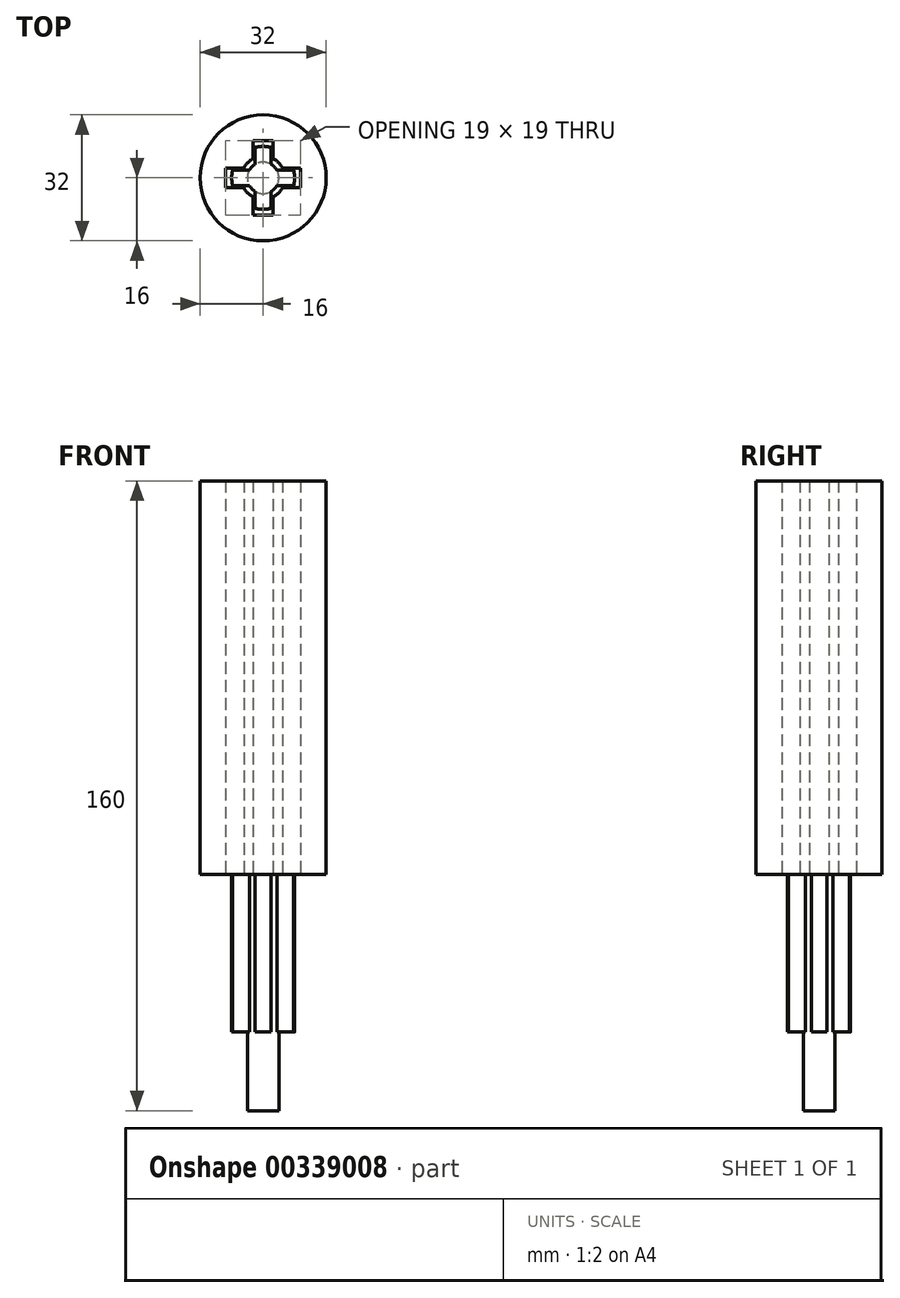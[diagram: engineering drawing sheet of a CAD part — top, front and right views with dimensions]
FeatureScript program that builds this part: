
annotation { "Feature Type Name" : "Feature", "Feature Type Description" : "" }
export const myFeature = defineFeature(function(context is Context, id is Id, definition is map)
    precondition{}
    {
        {
            var Q0;
            Q0=qCreatedBy(makeId("Top.planeOp"),FACE);
            var sketch = newSketch(context, id + "F0", { "sketchPlane" : qUnion([Q0])});
            skCircle(sketch, "E0", {"center": v(0, 0) * mm, "radius": 4 * mm});
            skSolve(sketch);
        }
        {
            var Q0;
            Q0=makeQuery(id+"F0.imprint","IMPRINT",FACE,{"disambiguationData":[TD([[makeQuery(id+"F0.imprint","IMPRINT",EDGE,{"derivedFrom":sQuery(id+"F0.wireOp",EDGE,"E0")}),1.0]])]});
            extrude(context, id + "F1", {"entities" : qUnion([Q0]), "depth" : 20 * mm});
        }
        {
            var Q0;
            Q0=makeQuery(id+"F1.opExtrude","CAP_FACE",FACE,{"disambiguationData":[OSD([sQuery(id+"F0.wireOp",EDGE,"E0")])],"isStart":false});
            cPlane(context, id + "F2", {"entities" : qUnion([Q0]), "cplaneType" : CPlaneType.OFFSET, "offset" : 0 * mm, "width" : 150 * mm, "height" : 150 * mm});
        }
        {
            var Q0;
            Q0=qCreatedBy(id+"F2.planeOp",FACE);
            var sketch = newSketch(context, id + "F3", { "sketchPlane" : qUnion([Q0])});
            skCircle(sketch, "E1", {"center": v(0, 0) * mm, "radius": 8 * mm, "construction": true});
            skCircle(sketch, "E2.0", {"center": v(0, 0) * mm, "radius": 4 * mm});
            skLineSegment(sketch, "E3", {"start": v(0, 4) * mm, "end": v(0, 8) * mm, "construction": true});
            skLineSegment(sketch, "E4", {"start": v(-2, 7.75) * mm, "end": v(-2, 3.46) * mm});
            skLineSegment(sketch, "E5.MirrorCS", {"start": v(2, 7.75) * mm, "end": v(2, 3.46) * mm});
            skLineSegment(sketch, "E6.1.1", {"start": v(-7.75, -2) * mm, "end": v(-3.46, -2) * mm});
            skLineSegment(sketch, "E6.1.3", {"start": v(-4, 0) * mm, "end": v(-8, 0) * mm, "construction": true});
            skLineSegment(sketch, "E6.1.4", {"start": v(-7.75, 2) * mm, "end": v(-3.46, 2) * mm});
            skLineSegment(sketch, "E6.2.1", {"start": v(2, -7.75) * mm, "end": v(2, -3.46) * mm});
            skLineSegment(sketch, "E6.2.3", {"start": v(0, -4) * mm, "end": v(0, -8) * mm, "construction": true});
            skLineSegment(sketch, "E6.2.4", {"start": v(-2, -7.75) * mm, "end": v(-2, -3.46) * mm});
            skLineSegment(sketch, "E6.3.1", {"start": v(7.75, 2) * mm, "end": v(3.46, 2) * mm});
            skLineSegment(sketch, "E6.3.3", {"start": v(4, 0) * mm, "end": v(8, 0) * mm, "construction": true});
            skLineSegment(sketch, "E6.3.4", {"start": v(7.75, -2) * mm, "end": v(3.46, -2) * mm});
            skArc(sketch, "E7", {"start": v(2, 7.75) * mm, "mid": v(0, 8) * mm, "end": v(-2, 7.75) * mm});
            skArc(sketch, "E8", {"start": v(7.75, -2) * mm, "mid": v(8, 0) * mm, "end": v(7.75, 2) * mm});
            skArc(sketch, "E9", {"start": v(-7.75, 2) * mm, "mid": v(-8, 0) * mm, "end": v(-7.75, -2) * mm});
            skArc(sketch, "E10", {"start": v(-2, -7.75) * mm, "mid": v(0, -8) * mm, "end": v(2, -7.75) * mm});
            skPoint(sketch, "E11.orphan", {"position": v(2, -8) * mm});
            skPoint(sketch, "E12.orphan", {"position": v(-2, -8) * mm});
            skPoint(sketch, "E13.orphan", {"position": v(8, -2) * mm});
            skPoint(sketch, "E14.orphan", {"position": v(8, 2) * mm});
            skPoint(sketch, "E15.orphan", {"position": v(2, 8) * mm});
            skPoint(sketch, "E16.MirrorCS.start.orphan", {"position": v(0, 8) * mm});
            skPoint(sketch, "E17.orphan", {"position": v(-2, 8) * mm});
            skPoint(sketch, "E18.orphan", {"position": v(-8, 2) * mm});
            skPoint(sketch, "E6.1.2.end.orphan", {"position": v(-8, -2) * mm});
            skSolve(sketch);
        }
        {
            var Q0;
            {var subQ0=sQuery(id+"F3.wireOp",EDGE,"E6.1.1");Q0=makeQuery(id+"F3.imprint","IMPRINT",FACE,{"disambiguationData":[TD([[makeQuery(id+"F3.imprint","IMPRINT",EDGE,{"derivedFrom":subQ0}),1.0]])]});}
            var Q1;
            {var subQ0=sQuery(id+"F3.wireOp",EDGE,"E2.0");var subQ4=makeQuery(id+"F3.imprint","INTERSECT",VERTEX,{"derivedFrom":[subQ0,sQuery(id+"F3.wireOp",EDGE,"E5.MirrorCS")]});Q1=makeQuery(id+"F3.imprint","IMPRINT",FACE,{"disambiguationData":[TD([[makeQuery(id+"F3.imprint","IMPRINT",EDGE,{"disambiguationData":[TD([[subQ4,1.0]])],"derivedFrom":subQ0}),1.0]])]});}
            var Q2;
            {var subQ0=sQuery(id+"F3.wireOp",EDGE,"E4");Q2=makeQuery(id+"F3.imprint","IMPRINT",FACE,{"disambiguationData":[TD([[makeQuery(id+"F3.imprint","IMPRINT",EDGE,{"derivedFrom":subQ0}),1.0]])]});}
            var Q3;
            {var subQ0=sQuery(id+"F3.wireOp",EDGE,"E6.3.1");Q3=makeQuery(id+"F3.imprint","IMPRINT",FACE,{"disambiguationData":[TD([[makeQuery(id+"F3.imprint","IMPRINT",EDGE,{"derivedFrom":subQ0}),1.0]])]});}
            var Q4;
            {var subQ0=sQuery(id+"F3.wireOp",EDGE,"E6.2.1");Q4=makeQuery(id+"F3.imprint","IMPRINT",FACE,{"disambiguationData":[TD([[makeQuery(id+"F3.imprint","IMPRINT",EDGE,{"derivedFrom":subQ0}),1.0]])]});}
            extrude(context, id + "F4", {"entities" : qUnion([Q0, Q1, Q2, Q3, Q4]), "operationType" : NewBodyOperationType.ADD, "depth" : 40 * mm});
        }
        {
            var Q0;
            Q0=makeQuery(id+"F4.opExtrude","CAP_FACE",FACE,{"disambiguationData":[OSD([sQuery(id+"F3.wireOp",EDGE,"E2.0"),sQuery(id+"F3.wireOp",EDGE,"E4"),sQuery(id+"F3.wireOp",EDGE,"E5.MirrorCS"),sQuery(id+"F3.wireOp",EDGE,"E6.1.1"),sQuery(id+"F3.wireOp",EDGE,"E6.1.4"),sQuery(id+"F3.wireOp",EDGE,"E6.2.1"),sQuery(id+"F3.wireOp",EDGE,"E6.2.4"),sQuery(id+"F3.wireOp",EDGE,"E6.3.1"),sQuery(id+"F3.wireOp",EDGE,"E6.3.4"),sQuery(id+"F3.wireOp",EDGE,"E7"),sQuery(id+"F3.wireOp",EDGE,"E8"),sQuery(id+"F3.wireOp",EDGE,"E9"),sQuery(id+"F3.wireOp",EDGE,"E10")])],"isStart":false});
            cPlane(context, id + "F5", {"entities" : qUnion([Q0]), "cplaneType" : CPlaneType.OFFSET, "offset" : 0 * mm, "width" : 150 * mm, "height" : 150 * mm});
        }
        {
            var Q0;
            Q0=qCreatedBy(id+"F5.planeOp",FACE);
            var sketch = newSketch(context, id + "F6", { "sketchPlane" : qUnion([Q0])});
            skCircle(sketch, "E19", {"center": v(0, 0) * mm, "radius": 16 * mm});
            skCircle(sketch, "E20", {"center": v(0, 0) * mm, "radius": 5.5 * mm});
            skLineSegment(sketch, "E21", {"start": v(0, 5.5) * mm, "end": v(0, 9.5) * mm, "construction": true});
            skLineSegment(sketch, "E22", {"start": v(0, 9.5) * mm, "end": v(-2.5, 9.5) * mm});
            skLineSegment(sketch, "E23", {"start": v(-2.5, 9.5) * mm, "end": v(-2.5, 4.9) * mm});
            skLineSegment(sketch, "E24.MirrorCS", {"start": v(0, 9.5) * mm, "end": v(2.5, 9.5) * mm});
            skLineSegment(sketch, "E25.MirrorCS", {"start": v(2.5, 9.5) * mm, "end": v(2.5, 4.9) * mm});
            skLineSegment(sketch, "E26.1.0", {"start": v(-9.5, 0) * mm, "end": v(-9.5, -2.5) * mm});
            skLineSegment(sketch, "E26.1.1", {"start": v(-9.5, 2.5) * mm, "end": v(-4.9, 2.5) * mm});
            skLineSegment(sketch, "E26.1.2", {"start": v(-9.5, 0) * mm, "end": v(-9.5, 2.5) * mm});
            skLineSegment(sketch, "E26.1.3", {"start": v(-9.5, -2.5) * mm, "end": v(-4.9, -2.5) * mm});
            skLineSegment(sketch, "E26.1.4", {"start": v(-5.5, 0) * mm, "end": v(-9.5, 0) * mm, "construction": true});
            skLineSegment(sketch, "E26.2.0", {"start": v(0, -9.5) * mm, "end": v(2.5, -9.5) * mm});
            skLineSegment(sketch, "E26.2.1", {"start": v(-2.5, -9.5) * mm, "end": v(-2.5, -4.9) * mm});
            skLineSegment(sketch, "E26.2.2", {"start": v(0, -9.5) * mm, "end": v(-2.5, -9.5) * mm});
            skLineSegment(sketch, "E26.2.3", {"start": v(2.5, -9.5) * mm, "end": v(2.5, -4.9) * mm});
            skLineSegment(sketch, "E26.2.4", {"start": v(0, -5.5) * mm, "end": v(0, -9.5) * mm, "construction": true});
            skLineSegment(sketch, "E26.3.0", {"start": v(9.5, 0) * mm, "end": v(9.5, 2.5) * mm});
            skLineSegment(sketch, "E26.3.1", {"start": v(9.5, -2.5) * mm, "end": v(4.9, -2.5) * mm});
            skLineSegment(sketch, "E26.3.2", {"start": v(9.5, 0) * mm, "end": v(9.5, -2.5) * mm});
            skLineSegment(sketch, "E26.3.3", {"start": v(9.5, 2.5) * mm, "end": v(4.9, 2.5) * mm});
            skLineSegment(sketch, "E26.3.4", {"start": v(5.5, 0) * mm, "end": v(9.5, 0) * mm, "construction": true});
            skSolve(sketch);
        }
        {
            var Q0;
            Q0=makeQuery(id+"F6.imprint","IMPRINT",FACE,{"disambiguationData":[TD([[makeQuery(id+"F6.imprint","IMPRINT",EDGE,{"derivedFrom":sQuery(id+"F6.wireOp",EDGE,"E19")}),1.0]])]});
            extrude(context, id + "F7", {"entities" : qUnion([Q0]), "depth" : 100 * mm});
        }
    });
